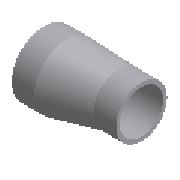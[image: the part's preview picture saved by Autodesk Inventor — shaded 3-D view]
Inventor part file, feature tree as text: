
AUTODESK INVENTOR PART (.ipt)
format: ipt  version: 2024.2 (Build 282272000, 272)  size: 203,776 bytes
history: native  units: mm (DEFAULTED — no unit token found)
features: other x5, revolve x2, loft x1
ambient origin geometry x8: Origin, YZ Plane, XZ Plane, XY Plane, X Axis, Y Axis, Z Axis, Center Point
bodies: Solid1 (feature_tree)
feature tree (8):
  revolve  "Revolve1"  [1 undecoded]
  revolve  "Revolve2"  [1 undecoded]
  loft  "Loft1"
  other  "Work Axis1"
  other  "Work Point1"
  other  "Work Axis2"
  other  "Work Point2"
  other  "Edges1"
note: 2 required parameter values undecoded (feature->parameter linkage not recoverable at this tier; creation-order binding heuristic only, values carry confidence <= 0.55)
